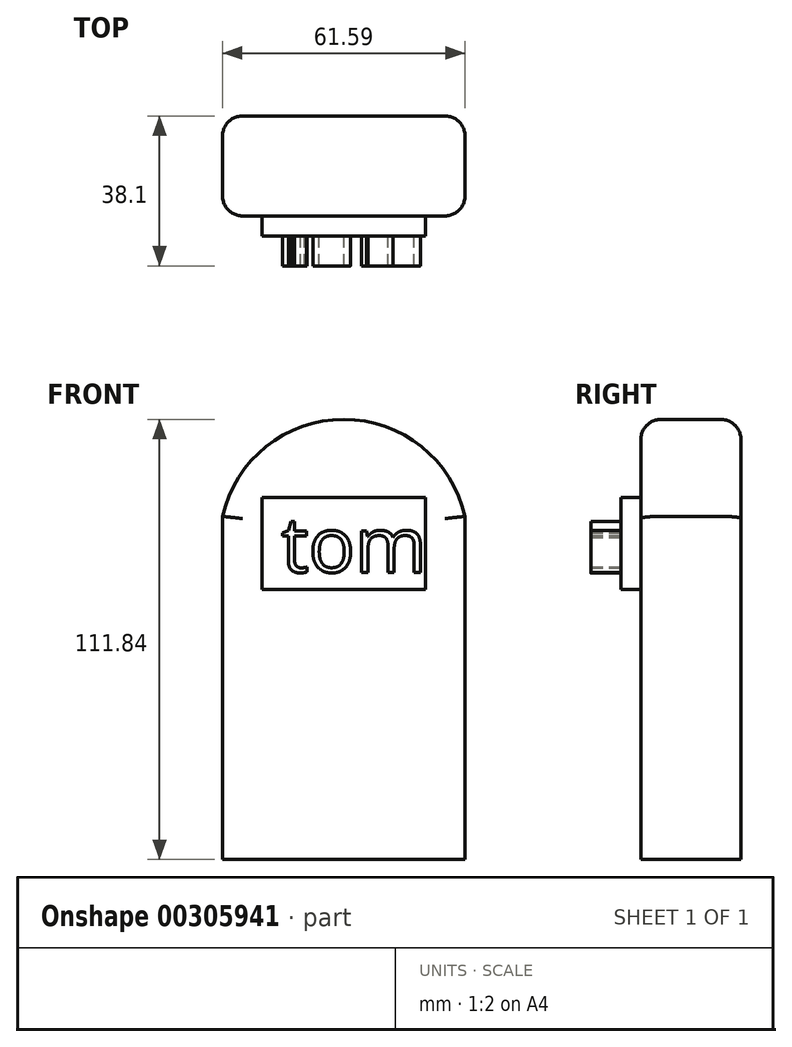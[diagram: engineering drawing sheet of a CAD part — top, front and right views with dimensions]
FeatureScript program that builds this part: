
annotation { "Feature Type Name" : "Feature", "Feature Type Description" : "" }
export const myFeature = defineFeature(function(context is Context, id is Id, definition is map)
    precondition{}
    {
        {
            var Q0;
            Q0=qCreatedBy(makeId("Front.planeOp"),FACE);
            var sketch = newSketch(context, id + "F0", { "sketchPlane" : qUnion([Q0])});
            skLineSegment(sketch, "E0.bottom", {"start": v(-35.69, 29.07) * mm, "end": v(25.9, 29.07) * mm});
            skLineSegment(sketch, "E0.top", {"start": v(-35.69, -58.14) * mm, "end": v(25.9, -58.14) * mm});
            skLineSegment(sketch, "E0.left", {"start": v(-35.69, 29.07) * mm, "end": v(-35.69, -58.14) * mm});
            skLineSegment(sketch, "E0.right", {"start": v(25.9, 29.07) * mm, "end": v(25.9, -58.14) * mm});
            skArc(sketch, "E1", {"start": v(25.9, 29.07) * mm, "mid": v(-4.9, 53.7) * mm, "end": v(-35.69, 29.07) * mm});
            skLineSegment(sketch, "E2.bottom", {"start": v(-21.87, 18.42) * mm, "end": v(12.09, 18.42) * mm});
            skLineSegment(sketch, "E2.top", {"start": v(-21.87, 25.85) * mm, "end": v(12.09, 25.85) * mm});
            skLineSegment(sketch, "E2.left", {"start": v(-21.87, 18.42) * mm, "end": v(-21.87, 25.85) * mm});
            skLineSegment(sketch, "E2.right", {"start": v(12.09, 18.42) * mm, "end": v(12.09, 25.85) * mm});
            skSolve(sketch);
        }
        {
            var Q0;
            Q0 = qSketchRegion(id + "F0", true);
            var Q1;
            Q1=makeQuery(id+"F0.imprint","IMPRINT",FACE,{"disambiguationData":[TD([[makeQuery(id+"F0.imprint","IMPRINT",EDGE,{"derivedFrom":sQuery(id+"F0.wireOp",EDGE,"E2.bottom")}),1.0]])]});
            extrude(context, id + "F1", {"entities" : qUnion([Q0, Q1]), "depth" : 25.4 * mm});
        }
        {
            var Q0;
            Q0=makeQuery(id+"F1.opExtrude","CAP_EDGE",EDGE,{"disambiguationData":[OSD([sQuery(id+"F0.wireOp",EDGE,"E0.left")])],"isStart":false});
            var Q1;
            Q1=makeQuery(id+"F1.opExtrude","CAP_EDGE",EDGE,{"disambiguationData":[OSD([sQuery(id+"F0.wireOp",EDGE,"E0.right")])],"isStart":false});
            var Q2;
            Q2=makeQuery(id+"F1.opExtrude","CAP_EDGE",EDGE,{"disambiguationData":[OSD([sQuery(id+"F0.wireOp",EDGE,"E0.right")])],"isStart":true});
            var Q3;
            Q3=makeQuery(id+"F1.opExtrude","CAP_EDGE",EDGE,{"disambiguationData":[OSD([sQuery(id+"F0.wireOp",EDGE,"E0.left")])],"isStart":true});
            var Q4;
            Q4=makeQuery(id+"F1.opExtrude","CAP_EDGE",EDGE,{"disambiguationData":[OSD([sQuery(id+"F0.wireOp",EDGE,"E1")])],"isStart":true});
            var Q5;
            Q5=makeQuery(id+"F1.opExtrude","CAP_EDGE",EDGE,{"disambiguationData":[OSD([sQuery(id+"F0.wireOp",EDGE,"E1")])],"isStart":false});
            fillet(context, id + "F2", {"entities" : qUnion([Q0, Q1, Q2, Q3, Q4, Q5]), "radius" : 5.08 * mm, "tangentPropagation" : true, "allowEdgeOverflow" : false});
        }
        {
            var Q0;
            Q0=makeQuery(id+"F1.opExtrude","CAP_FACE",FACE,{"disambiguationData":[OSD([sQuery(id+"F0.wireOp",EDGE,"E0.top"),sQuery(id+"F0.wireOp",EDGE,"E0.left"),sQuery(id+"F0.wireOp",EDGE,"E0.right"),sQuery(id+"F0.wireOp",EDGE,"E1")])],"isStart":false});
            var sketch = newSketch(context, id + "F3", { "sketchPlane" : qUnion([Q0])});
            skLineSegment(sketch, "E3.bottom", {"start": v(-25.62, 33.8) * mm, "end": v(15.84, 33.8) * mm});
            skLineSegment(sketch, "E3.top", {"start": v(-25.62, 10.48) * mm, "end": v(15.84, 10.48) * mm});
            skLineSegment(sketch, "E3.left", {"start": v(-25.62, 33.8) * mm, "end": v(-25.62, 10.48) * mm});
            skLineSegment(sketch, "E3.right", {"start": v(15.84, 33.8) * mm, "end": v(15.84, 10.48) * mm});
            skPoint(sketch, "E3.middle", {"position": v(-4.9, 22.14) * mm});
            skSolve(sketch);
        }
        {
            var Q0;
            Q0=makeQuery(id+"F3.imprint","IMPRINT",FACE,{"disambiguationData":[TD([[makeQuery(id+"F3.imprint","IMPRINT",EDGE,{"derivedFrom":sQuery(id+"F3.wireOp",EDGE,"E3.bottom")}),-1.0]])]});
            extrude(context, id + "F4", {"entities" : qUnion([Q0]), "operationType" : NewBodyOperationType.ADD, "depth" : 5.08 * mm});
        }
        {
            var Q0;
            Q0=makeQuery(id+"F4.opExtrude","CAP_FACE",FACE,{"disambiguationData":[OSD([sQuery(id+"F3.wireOp",EDGE,"E3.bottom"),sQuery(id+"F3.wireOp",EDGE,"E3.top"),sQuery(id+"F3.wireOp",EDGE,"E3.left"),sQuery(id+"F3.wireOp",EDGE,"E3.right")])],"isStart":false});
            var sketch = newSketch(context, id + "F5", { "sketchPlane" : qUnion([Q0])});
            skText(sketch, "E4", { "text": "tom\n", "fontName": "OpenSans-Regular.ttf"});
            const initialGuessF5  = {"E4": [-0.02078, 0.01486, 1, 0, 0.0141]};
            skSetInitialGuess(sketch, initialGuessF5);
            skSolve(sketch);
        }
        {
            var Q0;
            Q0 = qSketchRegion(id + "F5", true);
            extrude(context, id + "F6", {"entities" : qUnion([Q0]), "operationType" : NewBodyOperationType.ADD, "depth" : 7.62 * mm});
        }
    });
